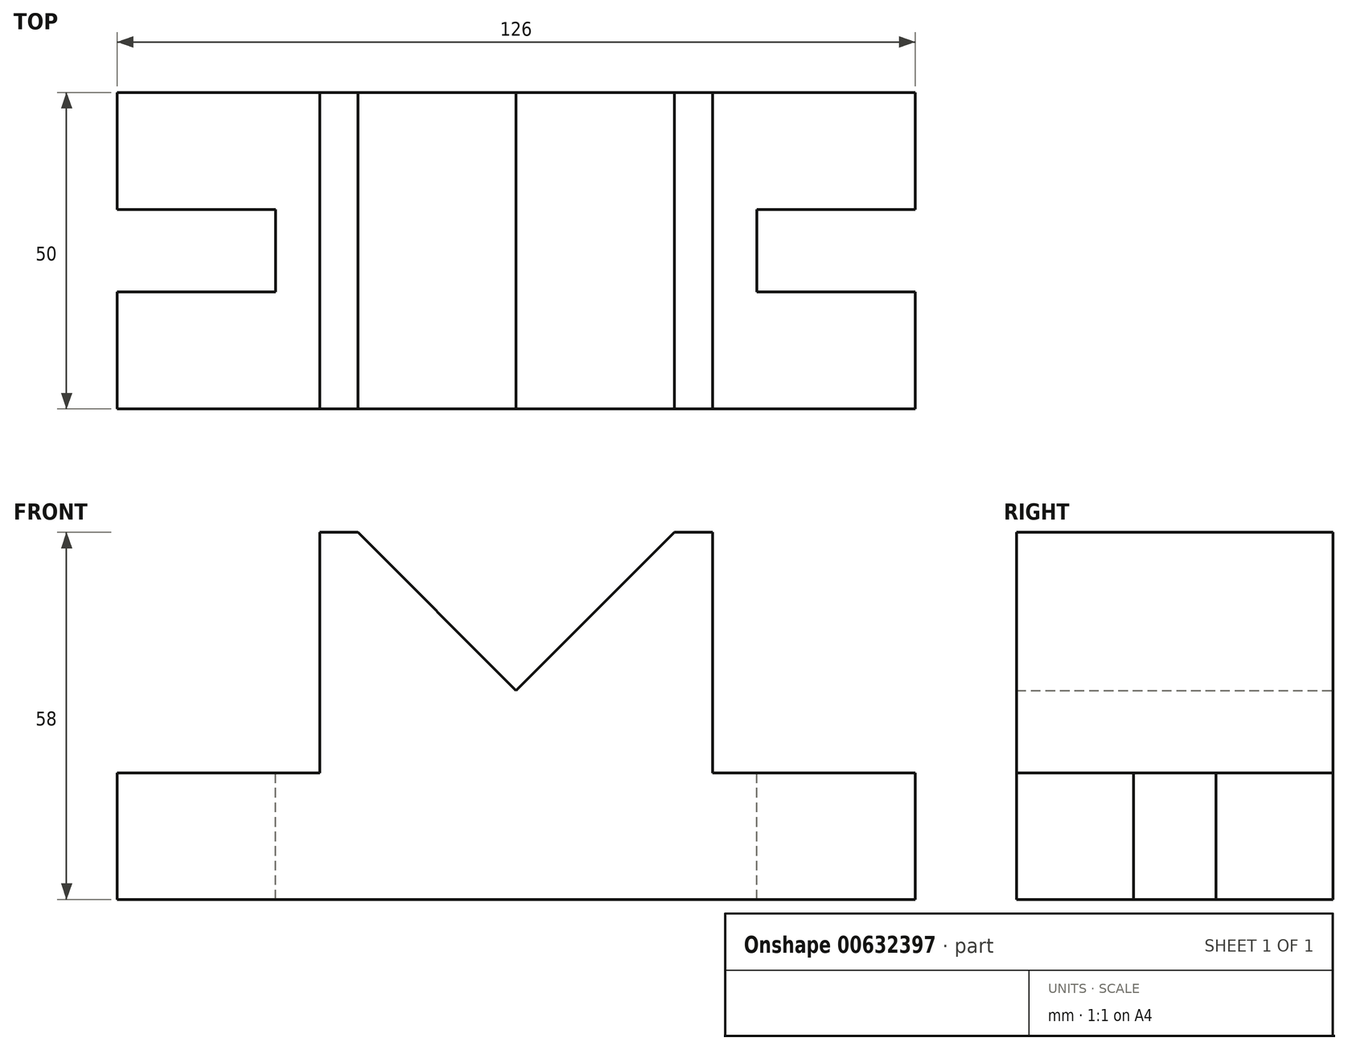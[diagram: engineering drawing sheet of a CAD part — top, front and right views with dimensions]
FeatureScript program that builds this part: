
annotation { "Feature Type Name" : "Feature", "Feature Type Description" : "" }
export const myFeature = defineFeature(function(context is Context, id is Id, definition is map)
    precondition{}
    {
        {
            var Q0;
            Q0=qCreatedBy(makeId("Front.planeOp"),FACE);
            var sketch = newSketch(context, id + "F0", { "sketchPlane" : qUnion([Q0])});
            skLineSegment(sketch, "E0", {"start": v(0, 0) * mm, "end": v(-63, 0) * mm});
            skLineSegment(sketch, "E1", {"start": v(0, 0) * mm, "end": v(63, 0) * mm});
            skLineSegment(sketch, "E2", {"start": v(63, 0) * mm, "end": v(63, 20) * mm});
            skLineSegment(sketch, "E3", {"start": v(63, 20) * mm, "end": v(31, 20) * mm});
            skLineSegment(sketch, "E4", {"start": v(31, 20) * mm, "end": v(31, 58) * mm});
            skLineSegment(sketch, "E5", {"start": v(31, 58) * mm, "end": v(25, 58) * mm});
            skLineSegment(sketch, "E6", {"start": v(25, 58) * mm, "end": v(0, 33) * mm});
            skLineSegment(sketch, "E7", {"start": v(0, 33) * mm, "end": v(-25, 58) * mm});
            skLineSegment(sketch, "E8", {"start": v(-25, 58) * mm, "end": v(-31, 58) * mm});
            skLineSegment(sketch, "E9", {"start": v(-31, 58) * mm, "end": v(-31, 20) * mm});
            skLineSegment(sketch, "E10", {"start": v(-31, 20) * mm, "end": v(-63, 20) * mm});
            skLineSegment(sketch, "E11", {"start": v(-63, 20) * mm, "end": v(-63, 0) * mm});
            skSolve(sketch);
        }
        {
            var Q0;
            Q0 = qSketchRegion(id + "F0", true);
            extrude(context, id + "F1", {"entities" : qUnion([Q0]), "depth" : 50 * mm, "offsetDistance" : 25 * mm});
        }
        {
            var Q0;
            Q0=makeQuery(id+"F1.opExtrude","SWEPT_FACE",FACE,{"disambiguationData":[OSD([sQuery(id+"F0.wireOp",EDGE,"E10")])]});
            var sketch = newSketch(context, id + "F2", { "sketchPlane" : qUnion([Q0])});
            skLineSegment(sketch, "E12", {"start": v(-63, -50) * mm, "end": v(-63, -31.5) * mm});
            skLineSegment(sketch, "E13", {"start": v(-63, -31.5) * mm, "end": v(-38, -31.5) * mm});
            skLineSegment(sketch, "E14", {"start": v(-38, -31.5) * mm, "end": v(-38, -18.5) * mm});
            skLineSegment(sketch, "E15", {"start": v(-38, -18.5) * mm, "end": v(-63, -18.5) * mm});
            skLineSegment(sketch, "E16", {"start": v(-63, -18.5) * mm, "end": v(-63, 0) * mm});
            skLineSegment(sketch, "E17.MirrorCS", {"start": v(38, -31.5) * mm, "end": v(38, -18.5) * mm});
            skLineSegment(sketch, "E18.MirrorCS", {"start": v(38, -18.5) * mm, "end": v(63, -18.5) * mm});
            skLineSegment(sketch, "E19.MirrorCS", {"start": v(63, -31.5) * mm, "end": v(38, -31.5) * mm});
            skLineSegment(sketch, "E20", {"start": v(63, -31.5) * mm, "end": v(63, -18.5) * mm});
            skSolve(sketch);
        }
        {
            var Q0;
            {var subQ0=sQuery(id+"F2.wireOp",EDGE,"E13");Q0=makeQuery(id+"F2.imprint","IMPRINT",FACE,{"disambiguationData":[TD([[makeQuery(id+"F2.imprint","IMPRINT",EDGE,{"derivedFrom":subQ0}),1.0]])]});}
            extrude(context, id + "F3", {"entities" : qUnion([Q0]), "operationType" : NewBodyOperationType.REMOVE, "endBound" : BoundingType.THROUGH_ALL, "oppositeDirection" : true, "depth" : 25 * mm, "offsetDistance" : 25 * mm});
        }
        {
            var Q0;
            Q0=makeQuery(id+"F2.imprint","IMPRINT",FACE,{"disambiguationData":[TD([[makeQuery(id+"F2.imprint","IMPRINT",EDGE,{"derivedFrom":sQuery(id+"F2.wireOp",EDGE,"E17.MirrorCS")}),-1.0]])]});
            extrude(context, id + "F4", {"entities" : qUnion([Q0]), "operationType" : NewBodyOperationType.REMOVE, "endBound" : BoundingType.THROUGH_ALL, "oppositeDirection" : true, "depth" : 25 * mm, "offsetDistance" : 25 * mm});
        }
    });
